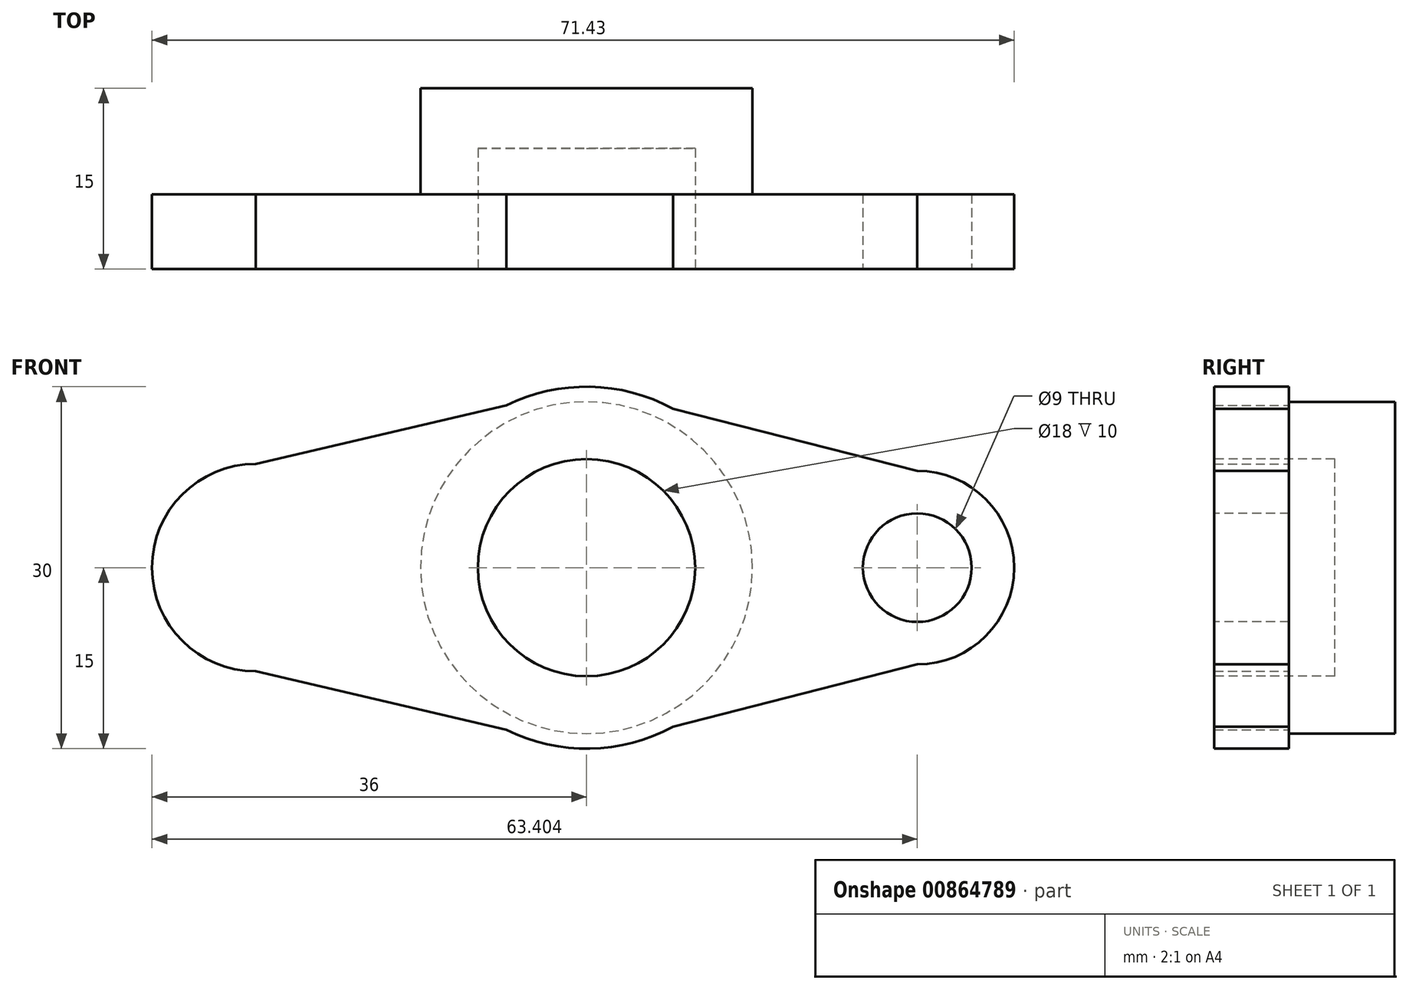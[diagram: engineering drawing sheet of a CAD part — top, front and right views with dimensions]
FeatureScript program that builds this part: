
annotation { "Feature Type Name" : "Feature", "Feature Type Description" : "" }
export const myFeature = defineFeature(function(context is Context, id is Id, definition is map)
    precondition{}
    {
        {
            var Q0;
            Q0=qCreatedBy(makeId("Front.planeOp"),FACE);
            var sketch = newSketch(context, id + "F0", { "sketchPlane" : qUnion([Q0])});
            skCircle(sketch, "E0", {"center": v(0, 0) * mm, "radius": 15 * mm});
            skLineSegment(sketch, "E1", {"start": v(0, 0) * mm, "end": v(27.4, 0) * mm});
            skLineSegment(sketch, "E2", {"start": v(0, 0) * mm, "end": v(-27.4, 0) * mm});
            skCircle(sketch, "E3", {"center": v(-27.4, 0) * mm, "radius": 8.6 * mm});
            skCircle(sketch, "E4", {"center": v(27.4, 0) * mm, "radius": 8.02 * mm});
            skLineSegment(sketch, "E5", {"start": v(27.4, 8.02) * mm, "end": v(0, 15) * mm});
            skLineSegment(sketch, "E6", {"start": v(0, 15) * mm, "end": v(-27.4, 8.6) * mm});
            skLineSegment(sketch, "E7", {"start": v(27.4, -8.02) * mm, "end": v(0, -15) * mm});
            skLineSegment(sketch, "E8", {"start": v(0, -15) * mm, "end": v(-27.4, -8.6) * mm});
            skSolve(sketch);
        }
        {
            var Q0;
            Q0 = qSketchRegion(id + "F0", true);
            extrude(context, id + "F1", {"entities" : qUnion([Q0]), "depth" : 6.2 * mm, "offsetDistance" : 25 * mm});
        }
        {
            var Q0;
            Q0=makeQuery(id+"F1.opExtrude","CAP_FACE",FACE,{"disambiguationData":[OSD([sQuery(id+"F0.wireOp",EDGE,"E0"),sQuery(id+"F0.wireOp",EDGE,"E3"),sQuery(id+"F0.wireOp",EDGE,"E4"),sQuery(id+"F0.wireOp",EDGE,"E5"),sQuery(id+"F0.wireOp",EDGE,"E6"),sQuery(id+"F0.wireOp",EDGE,"E7"),sQuery(id+"F0.wireOp",EDGE,"E8")])],"isStart":true});
            var sketch = newSketch(context, id + "F2", { "sketchPlane" : qUnion([Q0])});
            skCircle(sketch, "E9", {"center": v(0, 0) * mm, "radius": 13.75 * mm});
            skSolve(sketch);
        }
        {
            var Q0;
            Q0=makeQuery(id+"F2.imprint","IMPRINT",FACE,{"disambiguationData":[TD([[makeQuery(id+"F2.imprint","IMPRINT",EDGE,{"derivedFrom":sQuery(id+"F2.wireOp",EDGE,"E9")}),1.0]])]});
            extrude(context, id + "F3", {"entities" : qUnion([Q0]), "operationType" : NewBodyOperationType.ADD, "depth" : 8.8 * mm, "offsetDistance" : 25 * mm});
        }
        {
            var Q0;
            Q0=makeQuery(id+"F1.opExtrude","CAP_FACE",FACE,{"disambiguationData":[OSD([sQuery(id+"F0.wireOp",EDGE,"E0"),sQuery(id+"F0.wireOp",EDGE,"E3"),sQuery(id+"F0.wireOp",EDGE,"E4"),sQuery(id+"F0.wireOp",EDGE,"E5"),sQuery(id+"F0.wireOp",EDGE,"E6"),sQuery(id+"F0.wireOp",EDGE,"E7"),sQuery(id+"F0.wireOp",EDGE,"E8")])],"isStart":false});
            var sketch = newSketch(context, id + "F4", { "sketchPlane" : qUnion([Q0])});
            skCircle(sketch, "E10", {"center": v(0, 0) * mm, "radius": 13 * mm});
            skCircle(sketch, "E11", {"center": v(27.4, 0) * mm, "radius": 4.5 * mm});
            skCircle(sketch, "E12", {"center": v(-27.4, 0) * mm, "radius": 4.5 * mm});
            skCircle(sketch, "E13", {"center": v(0, 0) * mm, "radius": 9 * mm});
            skSolve(sketch);
        }
        {
            var Q0;
            Q0=makeQuery(id+"F4.imprint","IMPRINT",FACE,{"disambiguationData":[TD([[makeQuery(id+"F4.imprint","IMPRINT",EDGE,{"derivedFrom":sQuery(id+"F4.wireOp",EDGE,"E12")}),1.0]])]});
            var sketch = newSketch(context, id + "F5", { "sketchPlane" : qUnion([Q0])});
            skSolve(sketch);
        }
        {
            var Q0;
            Q0 = qSketchRegion(id + "F5", true);
            var Q1;
            Q1=makeQuery(id+"F4.imprint","IMPRINT",FACE,{"disambiguationData":[TD([[makeQuery(id+"F4.imprint","IMPRINT",EDGE,{"derivedFrom":sQuery(id+"F4.wireOp",EDGE,"E11")}),1.0]])]});
            var Q2;
            Q2=makeQuery(id+"F4.imprint","IMPRINT",FACE,{"disambiguationData":[TD([[makeQuery(id+"F4.imprint","IMPRINT",EDGE,{"derivedFrom":sQuery(id+"F4.wireOp",EDGE,"E13")}),1.0]])]});
            var Q3;
            Q3=makeQuery(id+"F5.imprint","IMPRINT",FACE,{"disambiguationData":[TD([[makeQuery(id+"F5.imprint","IMPRINT",EDGE,{"derivedFrom":makeQuery(id+"F4.imprint","IMPRINT",EDGE,{"derivedFrom":sQuery(id+"F4.wireOp",EDGE,"E12")})}),1.0]])]});
            extrude(context, id + "F6", {"entities" : qUnion([Q0, Q1, Q2, Q3]), "operationType" : NewBodyOperationType.REMOVE, "oppositeDirection" : true, "depth" : 10 * mm, "offsetDistance" : 25 * mm});
        }
    });
